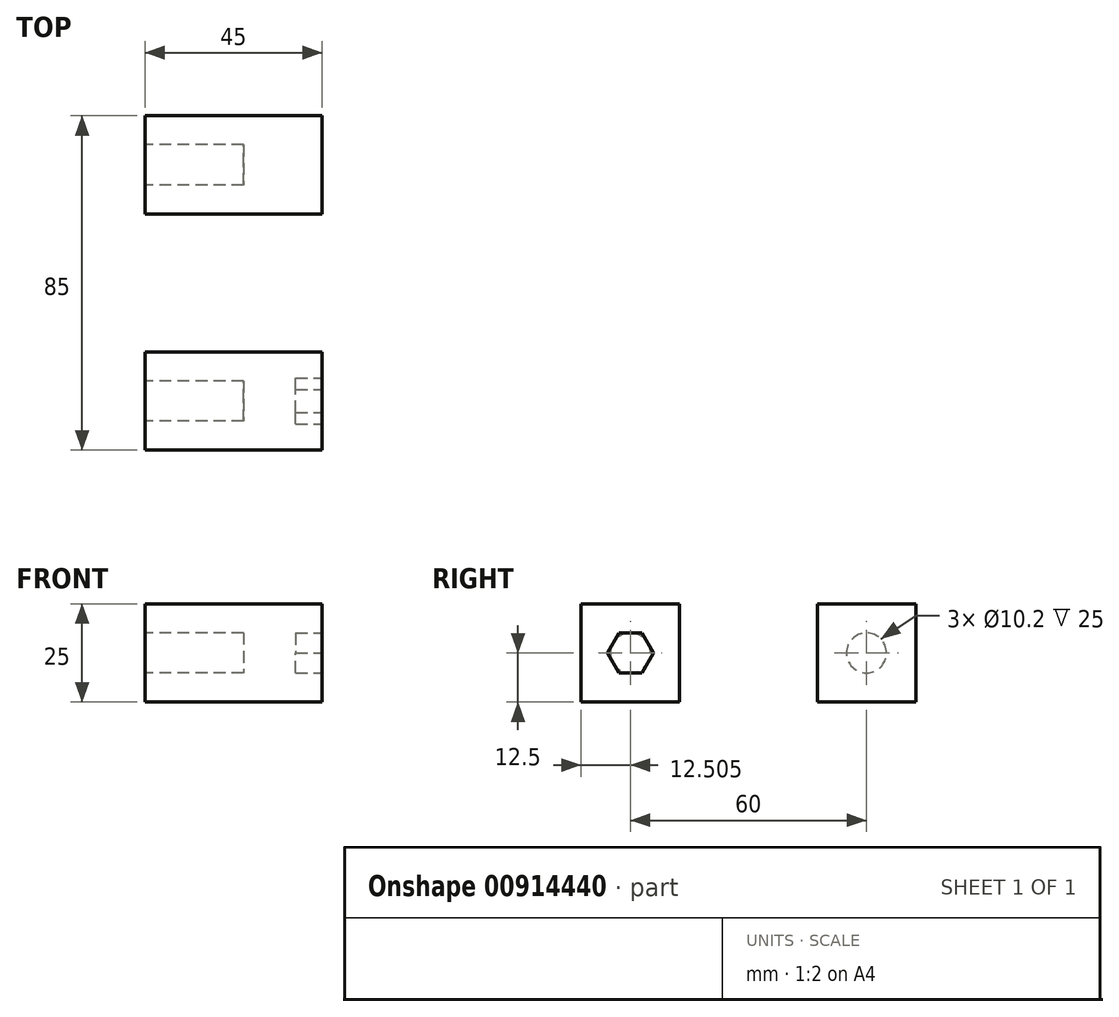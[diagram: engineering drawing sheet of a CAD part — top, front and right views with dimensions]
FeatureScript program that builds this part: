
annotation { "Feature Type Name" : "Feature", "Feature Type Description" : "" }
export const myFeature = defineFeature(function(context is Context, id is Id, definition is map)
    precondition{}
    {
        {
            var Q0;
            Q0=qCreatedBy(makeId("Top.planeOp"),FACE);
            var sketch = newSketch(context, id + "F0", { "sketchPlane" : qUnion([Q0])});
            skLineSegment(sketch, "E0.bottom", {"start": v(-10.06, 2) * mm, "end": v(34.94, 2) * mm});
            skLineSegment(sketch, "E0.top", {"start": v(-10.06, -23) * mm, "end": v(34.94, -23) * mm});
            skLineSegment(sketch, "E0.left", {"start": v(-10.06, 2) * mm, "end": v(-10.06, -23) * mm});
            skLineSegment(sketch, "E0.right", {"start": v(34.94, 2) * mm, "end": v(34.94, -23) * mm});
            skSolve(sketch);
        }
        {
            var Q0;
            Q0=makeQuery(id+"F0.imprint","IMPRINT",FACE,{"disambiguationData":[TD([[makeQuery(id+"F0.imprint","IMPRINT",EDGE,{"derivedFrom":sQuery(id+"F0.wireOp",EDGE,"E0.bottom")}),-1.0]])]});
            extrude(context, id + "F1", {"entities" : qUnion([Q0]), "depth" : 25 * mm, "offsetDistance" : 25 * mm});
        }
        {
            var Q0;
            Q0=makeQuery(id+"F1.opExtrude","SWEPT_FACE",FACE,{"disambiguationData":[OSD([sQuery(id+"F0.wireOp",EDGE,"E0.left")])]});
            var sketch = newSketch(context, id + "F2", { "sketchPlane" : qUnion([Q0])});
            skCircle(sketch, "E1", {"center": v(10.5, 12.5) * mm, "radius": 5.1 * mm});
            skLineSegment(sketch, "E2", {"start": v(23, 25) * mm, "end": v(-2, 0) * mm, "construction": true});
            skLineSegment(sketch, "E3", {"start": v(-2, 25) * mm, "end": v(23, 0) * mm, "construction": true});
            skSolve(sketch);
        }
        {
            var Q0;
            Q0=makeQuery(id+"F2.imprint","IMPRINT",FACE,{"disambiguationData":[TD([[makeQuery(id+"F2.imprint","IMPRINT",EDGE,{"derivedFrom":sQuery(id+"F2.wireOp",EDGE,"E1")}),1.0]])]});
            extrude(context, id + "F3", {"entities" : qUnion([Q0]), "operationType" : NewBodyOperationType.REMOVE, "oppositeDirection" : true, "depth" : 25 * mm, "offsetDistance" : 25 * mm});
        }
        {
            var Q0;
            Q0=makeQuery(id+"F1.opExtrude","SWEPT_BODY",BODY,{"disambiguationData":[OSD([sQuery(id+"F0.wireOp",EDGE,"E0.bottom"),sQuery(id+"F0.wireOp",EDGE,"E0.top"),sQuery(id+"F0.wireOp",EDGE,"E0.left"),sQuery(id+"F0.wireOp",EDGE,"E0.right")])]});
            transform(context, id + "F4", {"entities" : qUnion([Q0]), "transformType" : TransformType.TRANSLATION_3D, "dx" : 0 * mm, "dy" : 72 * mm, "dz" : 0 * mm, "makeCopy" : true});
        }
        {
            var Q0;
            Q0=makeQuery(id+"F1.opExtrude","SWEPT_FACE",FACE,{"disambiguationData":[OSD([sQuery(id+"F0.wireOp",EDGE,"E0.right")])]});
            var sketch = newSketch(context, id + "F5", { "sketchPlane" : qUnion([Q0])});
            skPoint(sketch, "E4.0", {"position": v(-10.5, 12.5) * mm});
            skCircle(sketch, "E5.cCircle", {"center": v(-10.5, 12.5) * mm, "radius": 5.05 * mm, "construction": true});
            skLineSegment(sketch, "E5.0", {"start": v(-7.58, 17.55) * mm, "end": v(-4.66, 12.5) * mm});
            skLineSegment(sketch, "E5.1", {"start": v(-4.66, 12.5) * mm, "end": v(-7.58, 7.45) * mm});
            skLineSegment(sketch, "E5.2", {"start": v(-7.58, 7.45) * mm, "end": v(-13.41, 7.45) * mm});
            skLineSegment(sketch, "E5.3", {"start": v(-13.41, 7.45) * mm, "end": v(-16.33, 12.5) * mm});
            skLineSegment(sketch, "E5.4", {"start": v(-16.33, 12.5) * mm, "end": v(-13.41, 17.55) * mm});
            skLineSegment(sketch, "E5.5", {"start": v(-13.41, 17.55) * mm, "end": v(-7.58, 17.55) * mm});
            skPoint(sketch, "E5.0.midPoint", {"position": v(-6.12, 15.02) * mm});
            skSolve(sketch);
        }
        {
            var Q0;
            Q0=makeQuery(id+"F4.opPattern","COPY",BODY,{"derivedFrom":makeQuery(id+"F1.opExtrude","SWEPT_BODY",BODY,{"disambiguationData":[OSD([sQuery(id+"F0.wireOp",EDGE,"E0.bottom"),sQuery(id+"F0.wireOp",EDGE,"E0.top"),sQuery(id+"F0.wireOp",EDGE,"E0.left"),sQuery(id+"F0.wireOp",EDGE,"E0.right")])]}),"instanceName":"1"});
            deleteBodies(context, id + "F6", {"entities" : qUnion([Q0])});
        }
        {
            var Q0;
            Q0=makeQuery(id+"F1.opExtrude","SWEPT_BODY",BODY,{"disambiguationData":[OSD([sQuery(id+"F0.wireOp",EDGE,"E0.bottom"),sQuery(id+"F0.wireOp",EDGE,"E0.top"),sQuery(id+"F0.wireOp",EDGE,"E0.left"),sQuery(id+"F0.wireOp",EDGE,"E0.right")])]});
            transform(context, id + "F7", {"entities" : qUnion([Q0]), "transformType" : TransformType.TRANSLATION_3D, "dx" : 0 * mm, "dy" : 60 * mm, "dz" : 0 * mm, "makeCopy" : true});
        }
        {
            var Q0;
            Q0=makeQuery(id+"F5.imprint","IMPRINT",FACE,{"disambiguationData":[TD([[makeQuery(id+"F5.imprint","IMPRINT",EDGE,{"derivedFrom":sQuery(id+"F5.wireOp",EDGE,"E5.0")}),-1.0]])]});
            extrude(context, id + "F8", {"entities" : qUnion([Q0]), "operationType" : NewBodyOperationType.REMOVE, "oppositeDirection" : true, "depth" : 6.8 * mm, "offsetDistance" : 25 * mm});
        }
        {
            var Q0;
            Q0=makeQuery(id+"F7.opPattern","COPY",BODY,{"derivedFrom":makeQuery(id+"F1.opExtrude","SWEPT_BODY",BODY,{"disambiguationData":[OSD([sQuery(id+"F0.wireOp",EDGE,"E0.bottom"),sQuery(id+"F0.wireOp",EDGE,"E0.top"),sQuery(id+"F0.wireOp",EDGE,"E0.left"),sQuery(id+"F0.wireOp",EDGE,"E0.right")])]}),"instanceName":"1"});
            transform(context, id + "F9", {"entities" : qUnion([Q0]), "transformType" : TransformType.TRANSLATION_3D, "dx" : 0 * mm, "dy" : 0 * mm, "dz" : 0 * mm, "makeCopy" : true});
        }
    });
